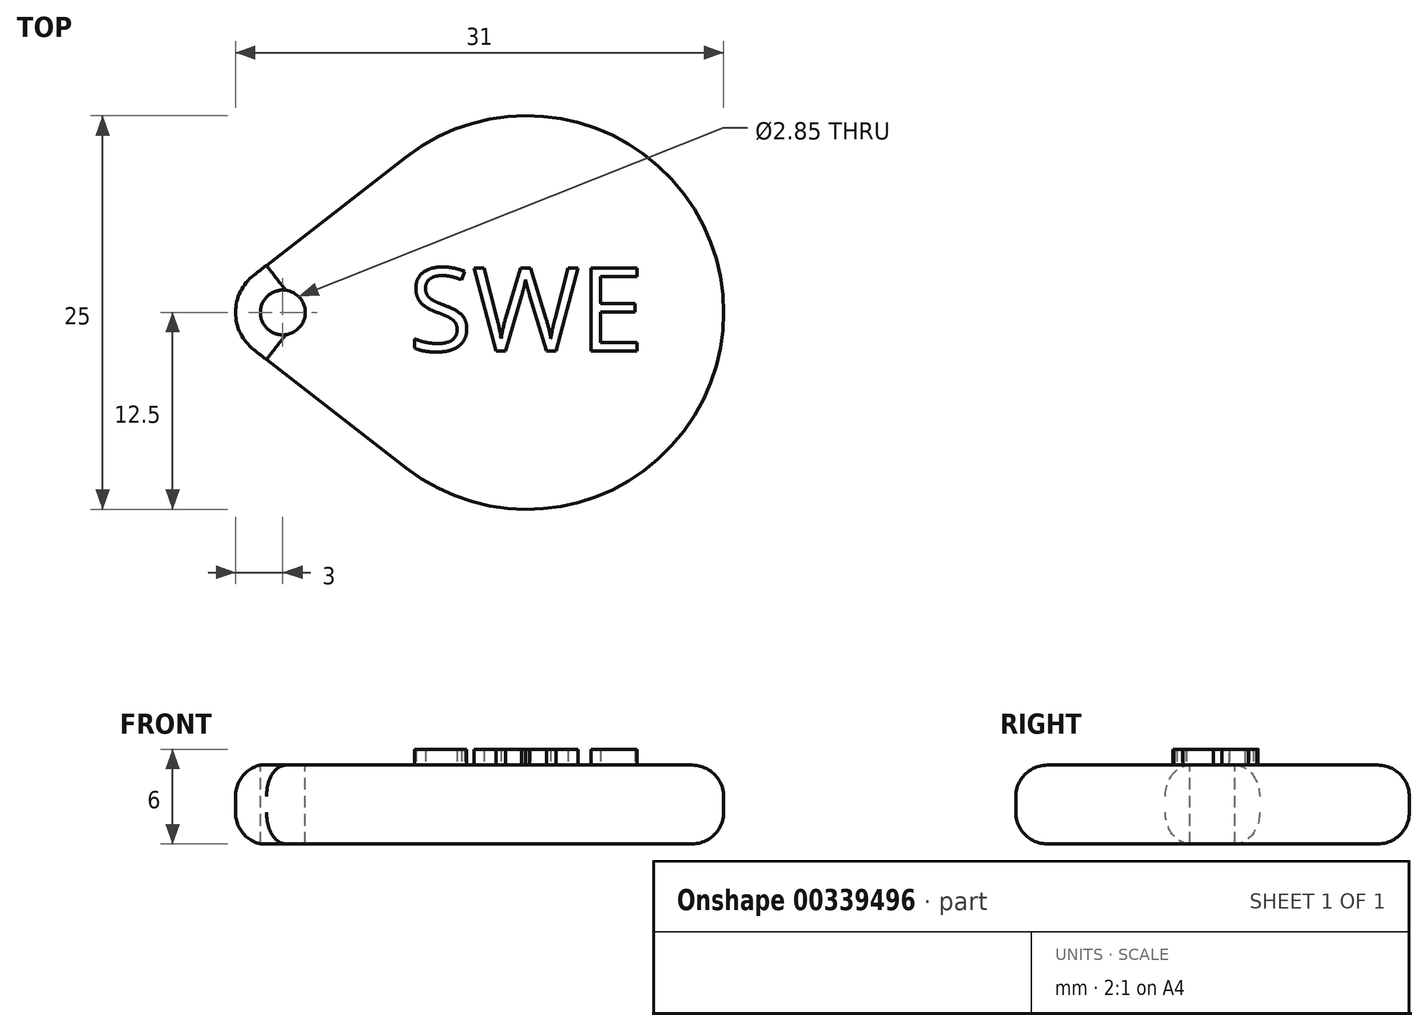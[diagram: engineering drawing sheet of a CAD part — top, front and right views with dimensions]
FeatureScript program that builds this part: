
annotation { "Feature Type Name" : "Feature", "Feature Type Description" : "" }
export const myFeature = defineFeature(function(context is Context, id is Id, definition is map)
    precondition{}
    {
        {
            var Q0;
            Q0=qCreatedBy(makeId("Top.planeOp"),FACE);
            var sketch = newSketch(context, id + "F0", { "sketchPlane" : qUnion([Q0])});
            skCircle(sketch, "E0", {"center": v(0, 0) * mm, "radius": 3 * mm});
            skCircle(sketch, "E1", {"center": v(15.5, 0) * mm, "radius": 12.5 * mm});
            skLineSegment(sketch, "E2", {"start": v(-1.84, 2.37) * mm, "end": v(7.84, 9.88) * mm});
            skLineSegment(sketch, "E3", {"start": v(-1.84, -2.37) * mm, "end": v(7.84, -9.88) * mm});
            skSolve(sketch);
        }
        {
            var Q0;
            Q0=qSketchRegion(id+"F0",true);
            extrude(context, id + "F1", {"entities" : qUnion([Q0]), "depth" : 2.5 * mm, "hasSecondDirection" : true, "secondDirectionOppositeDirection" : true, "secondDirectionDepth" : 2.5 * mm});
        }
        {
            var Q0;
            Q0=makeQuery(id+"F1.opExtrude","CAP_FACE",FACE,{"disambiguationData":[OSD([sQuery(id+"F0.wireOp",EDGE,"E0"),sQuery(id+"F0.wireOp",EDGE,"E1"),sQuery(id+"F0.wireOp",EDGE,"E2"),sQuery(id+"F0.wireOp",EDGE,"E3")])],"isStart":false});
            var sketch = newSketch(context, id + "F2", { "sketchPlane" : qUnion([Q0])});
            skCircle(sketch, "E4", {"center": v(0, 0) * mm, "radius": 1.42 * mm});
            skSolve(sketch);
        }
        {
            var Q0;
            Q0=qSketchRegion(id+"F2",true);
            var Q1;
            Q1=makeQuery(id+"F1.opExtrude","CAP_FACE",FACE,{"disambiguationData":[OSD([sQuery(id+"F0.wireOp",EDGE,"E0"),sQuery(id+"F0.wireOp",EDGE,"E1"),sQuery(id+"F0.wireOp",EDGE,"E2"),sQuery(id+"F0.wireOp",EDGE,"E3")])],"isStart":true});
            extrude(context, id + "F3", {"entities" : qUnion([Q0]), "operationType" : NewBodyOperationType.REMOVE, "endBound" : BoundingType.UP_TO_SURFACE, "oppositeDirection" : true, "endBoundEntityFace" : qUnion([Q1]), "depth" : 25 * mm});
        }
        {
            var Q0;
            Q0=makeQuery(id+"F1.opExtrude","CAP_FACE",FACE,{"disambiguationData":[OSD([sQuery(id+"F0.wireOp",EDGE,"E0"),sQuery(id+"F0.wireOp",EDGE,"E1"),sQuery(id+"F0.wireOp",EDGE,"E2"),sQuery(id+"F0.wireOp",EDGE,"E3")])],"isStart":false});
            var sketch = newSketch(context, id + "F4", { "sketchPlane" : qUnion([Q0])});
            skText(sketch, "E5", { "text": "SWE", "fontName": "OpenSans-Regular.ttf"});
            const initialGuessF4  = {"E5": [0.008, -0.00244, 1, 0, 0.0053]};
            skSetInitialGuess(sketch, initialGuessF4);
            skSolve(sketch);
        }
        {
            var Q0;
            Q0=qSketchRegion(id+"F4",true);
            extrude(context, id + "F5", {"entities" : qUnion([Q0]), "operationType" : NewBodyOperationType.ADD, "depth" : 1 * mm});
        }
        {
            var Q0;
            Q0=makeQuery(id+"F1.opExtrude","CAP_EDGE",EDGE,{"disambiguationData":[OSD([sQuery(id+"F0.wireOp",EDGE,"E3")])],"isStart":true});
            var Q1;
            Q1=makeQuery(id+"F1.opExtrude","CAP_EDGE",EDGE,{"disambiguationData":[OSD([sQuery(id+"F0.wireOp",EDGE,"E2")])],"isStart":true});
            var Q2;
            Q2=makeQuery(id+"F1.opExtrude","CAP_EDGE",EDGE,{"disambiguationData":[OSD([sQuery(id+"F0.wireOp",EDGE,"E1")])],"isStart":true});
            var Q3;
            Q3=makeQuery(id+"F1.opExtrude","CAP_EDGE",EDGE,{"disambiguationData":[OSD([sQuery(id+"F0.wireOp",EDGE,"E2")])],"isStart":false});
            var Q4;
            Q4=makeQuery(id+"F1.opExtrude","CAP_EDGE",EDGE,{"disambiguationData":[OSD([sQuery(id+"F0.wireOp",EDGE,"E1")])],"isStart":false});
            var Q5;
            Q5=makeQuery(id+"F1.opExtrude","CAP_EDGE",EDGE,{"disambiguationData":[OSD([sQuery(id+"F0.wireOp",EDGE,"E3")])],"isStart":false});
            var Q6;
            Q6=makeQuery(id+"F1.opExtrude","CAP_EDGE",EDGE,{"disambiguationData":[OSD([sQuery(id+"F0.wireOp",EDGE,"E0")])],"isStart":false});
            fillet(context, id + "F6", {"entities" : qUnion([Q0, Q1, Q2, Q3, Q4, Q5, Q6]), "radius" : 2 * mm, "tangentPropagation" : true, "allowEdgeOverflow" : false});
        }
    });
